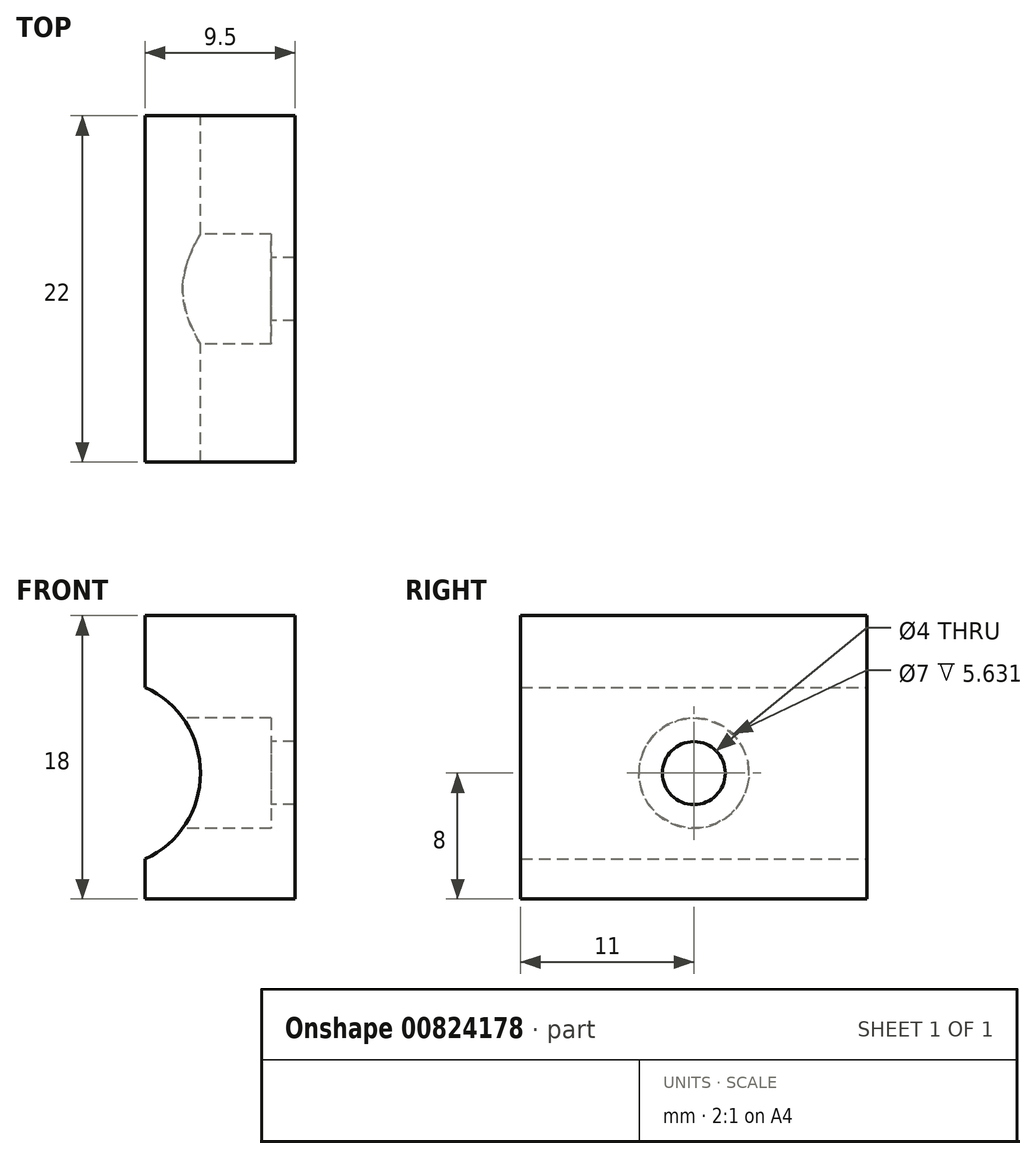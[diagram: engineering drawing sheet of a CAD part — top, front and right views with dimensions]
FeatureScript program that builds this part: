
annotation { "Feature Type Name" : "Feature", "Feature Type Description" : "" }
export const myFeature = defineFeature(function(context is Context, id is Id, definition is map)
    precondition{}
    {
        {
            var Q0;
            Q0=qCreatedBy(makeId("Front.planeOp"),FACE);
            var sketch = newSketch(context, id + "F0", { "sketchPlane" : qUnion([Q0])});
            skLineSegment(sketch, "E0", {"start": v(-45.4, -26.2) * mm, "end": v(6.33, -26.2) * mm, "construction": true});
            skLineSegment(sketch, "E1", {"start": v(-45.4, -26.2) * mm, "end": v(-45.4, 34.65) * mm, "construction": true});
            skLineSegment(sketch, "E2", {"start": v(-45.4, 0) * mm, "end": v(-0.1, 0) * mm, "construction": true});
            skLineSegment(sketch, "E3", {"start": v(-45.4, 32.76) * mm, "end": v(-17.41, 32.76) * mm, "construction": true});
            skLineSegment(sketch, "E4", {"start": v(-17.5, 34.65) * mm, "end": v(-17.5, 13.45) * mm, "construction": true});
            skPoint(sketch, "E4.endSnap0", {"position": v(-19.53, -26.2) * mm});
            skLineSegment(sketch, "E5", {"start": v(-17.5, 8) * mm, "end": v(-41.19, 8) * mm, "construction": true});
            skPoint(sketch, "E6", {"position": v(-17.5, 18) * mm});
            skPoint(sketch, "E7", {"position": v(0, 0) * mm});
            skLineSegment(sketch, "E8.bottom", {"start": v(-17.5, 18) * mm, "end": v(0, 18) * mm});
            skLineSegment(sketch, "E8.top", {"start": v(-17.5, 0) * mm, "end": v(0, 0) * mm});
            skLineSegment(sketch, "E8.left", {"start": v(-17.5, 18) * mm, "end": v(-17.5, 13.45) * mm});
            skLineSegment(sketch, "E8.right", {"start": v(0, 18) * mm, "end": v(0, 0) * mm});
            skPoint(sketch, "E9", {"position": v(-20, 8) * mm});
            skLineSegment(sketch, "E10", {"start": v(-17.5, 8) * mm, "end": v(0, 8) * mm, "construction": true});
            skArc(sketch, "E11", {"start": v(-17.5, 2.55) * mm, "mid": v(-14, 8) * mm, "end": v(-17.5, 13.45) * mm});
            skLineSegment(sketch, "E12.trimOffspring", {"start": v(-17.5, 2.55) * mm, "end": v(-17.5, -26.2) * mm, "construction": true});
            skLineSegment(sketch, "E13.trimOffspring", {"start": v(-17.5, 2.55) * mm, "end": v(-17.5, 0) * mm});
            skSolve(sketch);
        }
        {
            var Q0;
            Q0=makeQuery(id+"F0.imprint","IMPRINT",FACE,{"disambiguationData":[TD([[makeQuery(id+"F0.imprint","IMPRINT",EDGE,{"derivedFrom":sQuery(id+"F0.wireOp",EDGE,"E8.bottom")}),-1.0]])]});
            var Q1;
            Q1 = qConstructionFilter(qBodyType(qCreatedBy(id + "F0" ,EDGE), BodyType.WIRE), ConstructionObject.NO);
            extrude(context, id + "F1", {"entities" : qUnion([Q0]), "surfaceEntities" : qUnion([Q1]), "depth" : 22 * mm, "offsetDistance" : 25 * mm});
        }
        {
            var Q0;
            Q0=makeQuery(id+"F1.opExtrude","SWEPT_FACE",FACE,{"disambiguationData":[OSD([sQuery(id+"F0.wireOp",EDGE,"E13.trimOffspring")])]});
            var sketch = newSketch(context, id + "F2", { "sketchPlane" : qUnion([Q0])});
            skLineSegment(sketch, "E14", {"start": v(0, 0) * mm, "end": v(24.31, 0) * mm, "construction": true});
            skLineSegment(sketch, "E15", {"start": v(0, 0) * mm, "end": v(0, 45.04) * mm, "construction": true});
            skLineSegment(sketch, "E16", {"start": v(11, 0) * mm, "end": v(11, 44.4) * mm, "construction": true});
            skCircle(sketch, "E17", {"center": v(11, 8) * mm, "radius": 2 * mm});
            skSolve(sketch);
        }
        {
            var Q0;
            Q0 = qSketchRegion(id + "F2", true);
            extrude(context, id + "F3", {"entities" : qUnion([Q0]), "operationType" : NewBodyOperationType.REMOVE, "oppositeDirection" : true, "depth" : 25 * mm, "offsetDistance" : 25 * mm});
        }
        {
            var Q0;
            Q0=makeQuery(id+"F1.opExtrude","SWEPT_FACE",FACE,{"disambiguationData":[OSD([sQuery(id+"F0.wireOp",EDGE,"E8.left")])]});
            var sketch = newSketch(context, id + "F4", { "sketchPlane" : qUnion([Q0])});
            skSolve(sketch);
        }
        {
            var Q0;
            {var subQ0=sQuery(id+"F0.wireOp",EDGE,"E8.left");Q0=makeQuery(id+"F4.imprint","IMPRINT",FACE,{"disambiguationData":[TD([[makeQuery(id+"F4.imprint","IMPRINT",EDGE,{"derivedFrom":makeQuery(id+"F1.opExtrude","CAP_EDGE",EDGE,{"disambiguationData":[OSD([subQ0])],"isStart":true})}),1.0]])]});}
            var sketch = newSketch(context, id + "F5", { "sketchPlane" : qUnion([Q0])});
            skLineSegment(sketch, "E18", {"start": v(0, 0) * mm, "end": v(19.1, 0) * mm, "construction": true});
            skLineSegment(sketch, "E19", {"start": v(0, 0) * mm, "end": v(0, 22.82) * mm, "construction": true});
            skLineSegment(sketch, "E20", {"start": v(11, 0) * mm, "end": v(11, 14.13) * mm, "construction": true});
            skLineSegment(sketch, "E21", {"start": v(0, 8) * mm, "end": v(21.37, 8) * mm, "construction": true});
            skCircle(sketch, "E22", {"center": v(11, 8) * mm, "radius": 3.5 * mm});
            skSolve(sketch);
        }
        {
            var Q0;
            Q0 = qSketchRegion(id + "F5", true);
            extrude(context, id + "F6", {"entities" : qUnion([Q0]), "operationType" : NewBodyOperationType.REMOVE, "oppositeDirection" : true, "depth" : 8 * mm, "offsetDistance" : 25 * mm});
        }
        {
            var Q0;
            Q0=makeQuery(id+"F1.opExtrude","SWEPT_FACE",FACE,{"disambiguationData":[OSD([sQuery(id+"F0.wireOp",EDGE,"E8.bottom")])]});
            var sketch = newSketch(context, id + "F7", { "sketchPlane" : qUnion([Q0])});
            skLineSegment(sketch, "E23.bottom", {"start": v(0, 0) * mm, "end": v(-8, 0) * mm});
            skLineSegment(sketch, "E23.top", {"start": v(0, -22) * mm, "end": v(-8, -22) * mm});
            skLineSegment(sketch, "E23.left", {"start": v(0, 0) * mm, "end": v(0, -22) * mm});
            skLineSegment(sketch, "E23.right", {"start": v(-8, 0) * mm, "end": v(-8, -22) * mm});
            skSolve(sketch);
        }
        {
            var Q0;
            Q0 = qSketchRegion(id + "F7", true);
            extrude(context, id + "F8", {"entities" : qUnion([Q0]), "operationType" : NewBodyOperationType.REMOVE, "oppositeDirection" : true, "depth" : 25 * mm, "offsetDistance" : 25 * mm});
        }
    });
